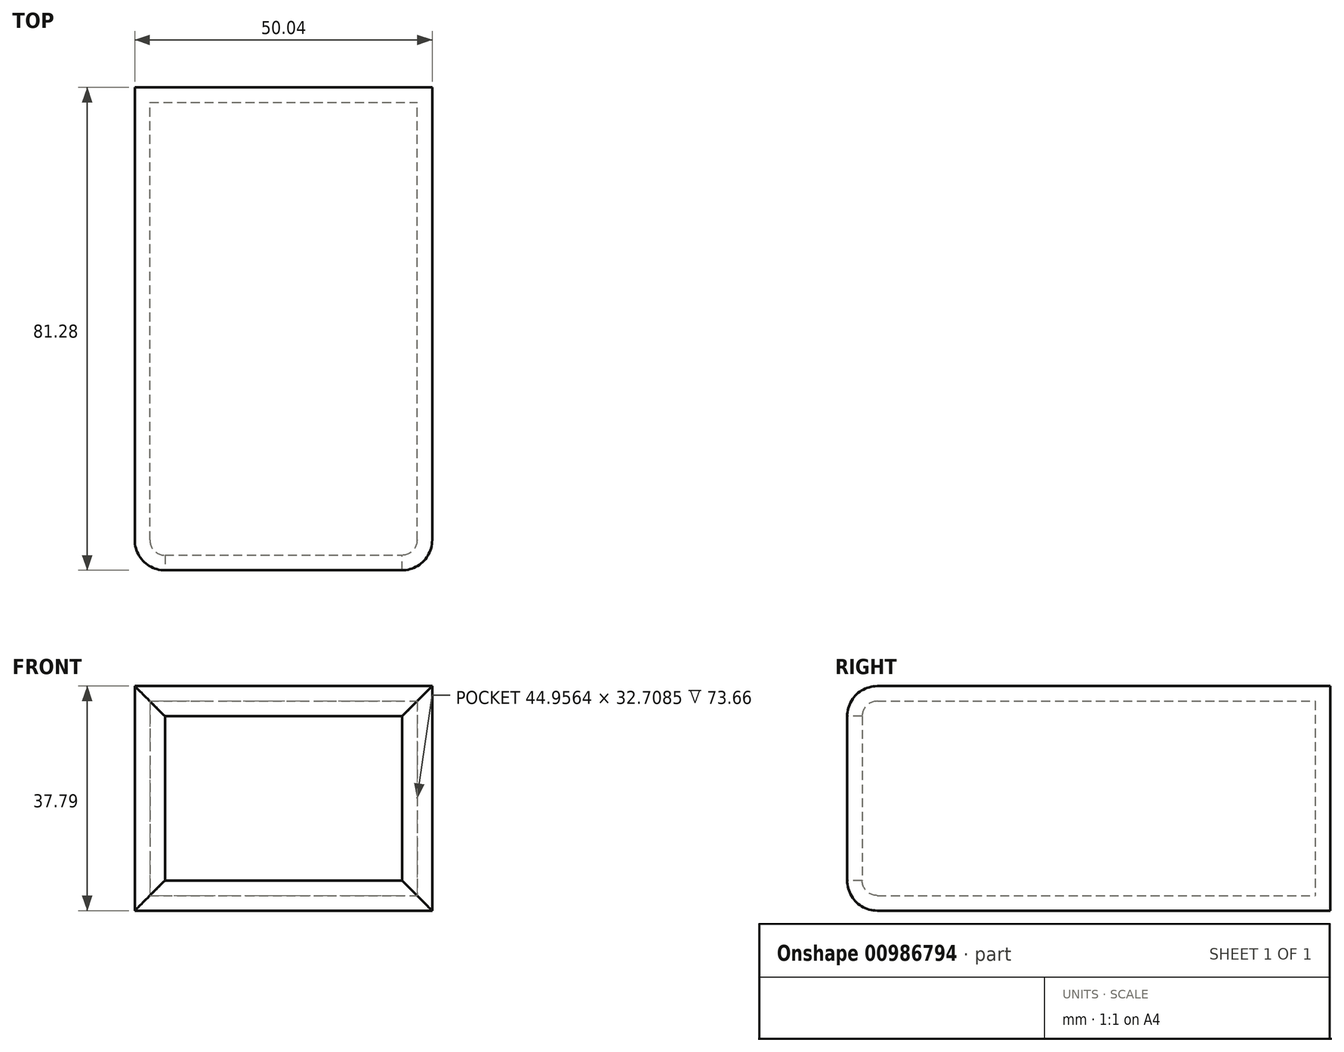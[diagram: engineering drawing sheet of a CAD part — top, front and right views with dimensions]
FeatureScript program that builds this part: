
annotation { "Feature Type Name" : "Feature", "Feature Type Description" : "" }
export const myFeature = defineFeature(function(context is Context, id is Id, definition is map)
    precondition{}
    {
        {
            var Q0;
            Q0=qCreatedBy(makeId("Front.planeOp"),FACE);
            var sketch = newSketch(context, id + "F0", { "sketchPlane" : qUnion([Q0])});
            skLineSegment(sketch, "E0.bottom", {"start": v(0, 0) * mm, "end": v(50.04, 0) * mm});
            skLineSegment(sketch, "E0.top", {"start": v(0, -37.79) * mm, "end": v(50.04, -37.79) * mm});
            skLineSegment(sketch, "E0.left", {"start": v(0, 0) * mm, "end": v(0, -37.79) * mm});
            skLineSegment(sketch, "E0.right", {"start": v(50.04, 0) * mm, "end": v(50.04, -37.79) * mm});
            skSolve(sketch);
        }
        {
            var Q0;
            Q0 = qSketchRegion(id + "F0", true);
            extrude(context, id + "F1", {"entities" : qUnion([Q0]), "depth" : 81.28 * mm, "offsetDistance" : 25.4 * mm});
        }
        {
            var Q0;
            Q0=makeQuery(id+"F1.opExtrude","CAP_FACE",FACE,{"disambiguationData":[OSD([sQuery(id+"F0.wireOp",EDGE,"E0.bottom"),sQuery(id+"F0.wireOp",EDGE,"E0.top"),sQuery(id+"F0.wireOp",EDGE,"E0.left"),sQuery(id+"F0.wireOp",EDGE,"E0.right")])],"isStart":false});
            fillet(context, id + "F2", {"entities" : qUnion([Q0]), "radius" : 5.08 * mm, "tangentPropagation" : true, "allowEdgeOverflow" : false});
        }
        {
            var Q0;
            Q0=makeQuery(id+"F1.opExtrude","CAP_FACE",FACE,{"disambiguationData":[OSD([sQuery(id+"F0.wireOp",EDGE,"E0.bottom"),sQuery(id+"F0.wireOp",EDGE,"E0.top"),sQuery(id+"F0.wireOp",EDGE,"E0.left"),sQuery(id+"F0.wireOp",EDGE,"E0.right")])],"isStart":false});
            shell(context, id + "F3", {"entities" : qUnion([Q0]), "thickness" : 2.54 * mm});
        }
    });
